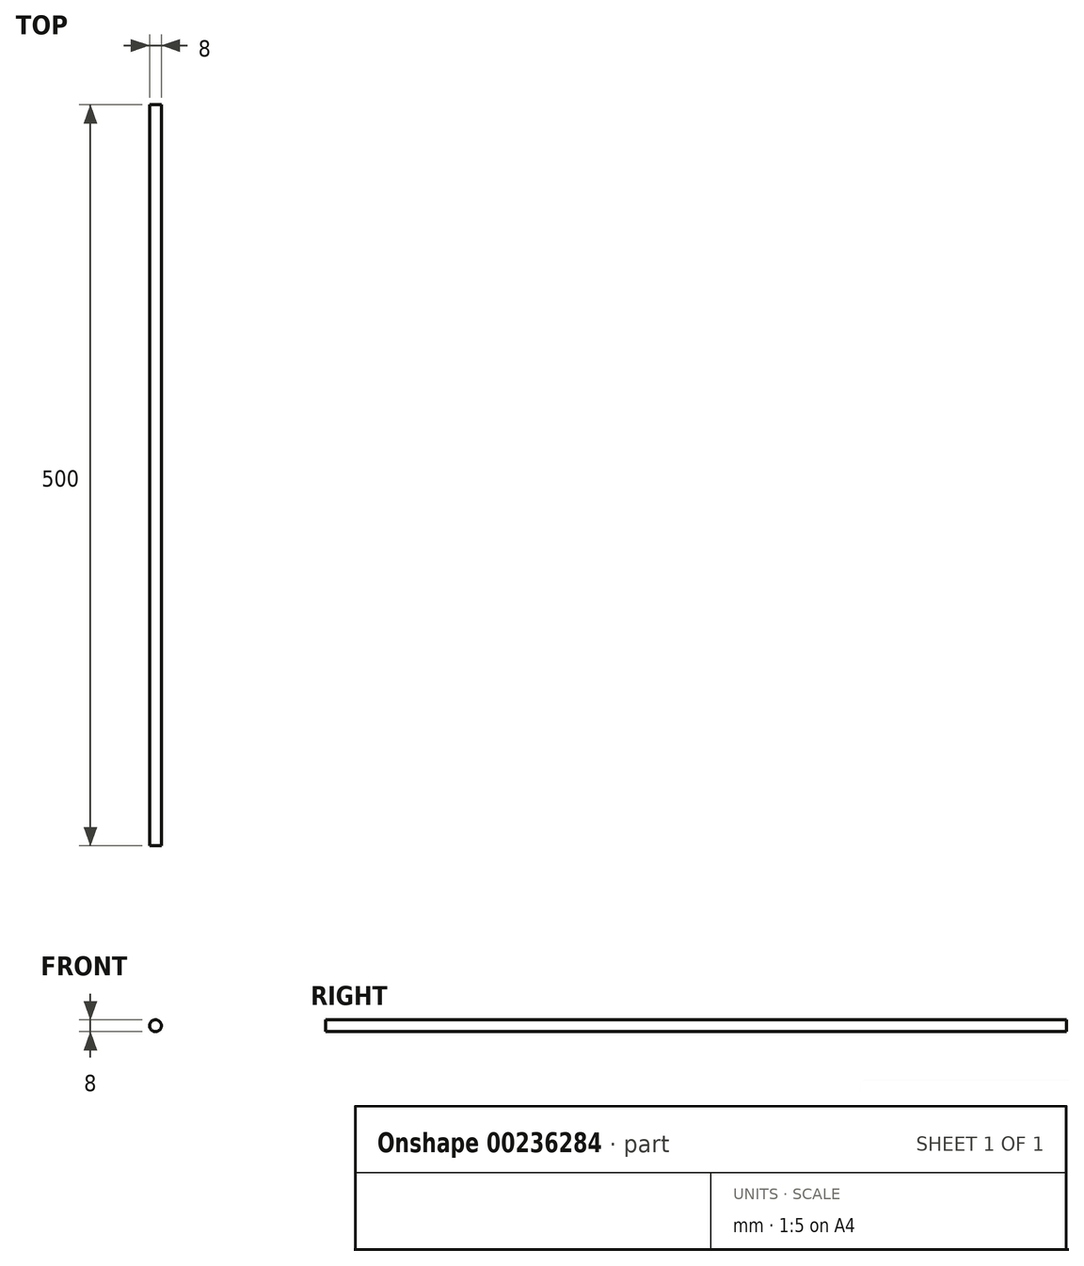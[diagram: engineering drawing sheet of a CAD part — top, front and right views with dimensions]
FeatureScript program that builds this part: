
annotation { "Feature Type Name" : "Feature", "Feature Type Description" : "" }
export const myFeature = defineFeature(function(context is Context, id is Id, definition is map)
    precondition{}
    {
        {
            var Q0;
            Q0=qCreatedBy(makeId("Front.planeOp"),FACE);
            var sketch = newSketch(context, id + "F0", { "sketchPlane" : qUnion([Q0])});
            skCircle(sketch, "E0", {"center": v(0, 0) * mm, "radius": 4 * mm});
            skSolve(sketch);
        }
        {
            var Q0;
            Q0 = qSketchRegion(id + "F0", true);
            extrude(context, id + "F1", {"entities" : qUnion([Q0]), "depth" : 500 * mm});
        }
    });
